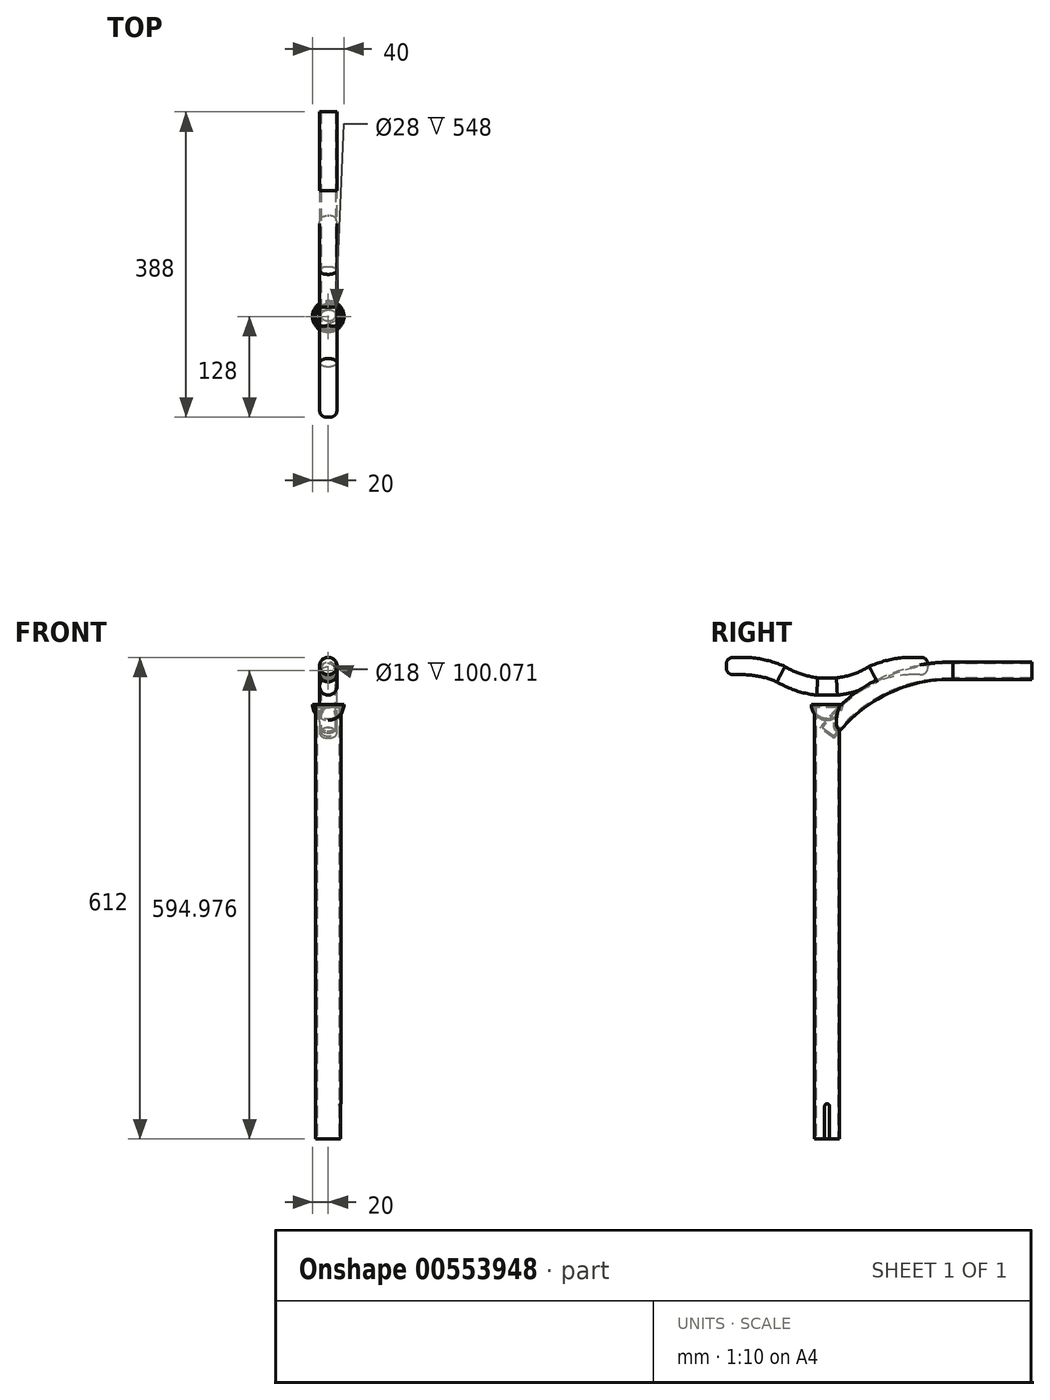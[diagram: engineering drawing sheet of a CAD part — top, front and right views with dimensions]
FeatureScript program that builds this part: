
annotation { "Feature Type Name" : "Feature", "Feature Type Description" : "" }
export const myFeature = defineFeature(function(context is Context, id is Id, definition is map)
    precondition{}
    {
        {
            var Q0;
            Q0=qCreatedBy(makeId("Top.planeOp"),FACE);
            var sketch = newSketch(context, id + "F0", { "sketchPlane" : qUnion([Q0])});
            skCircle(sketch, "E0", {"center": v(0, 0) * mm, "radius": 16 * mm});
            skSolve(sketch);
        }
        {
            var Q0;
            Q0 = qSketchRegion(id + "F0", true);
            extrude(context, id + "F1", {"entities" : qUnion([Q0]), "depth" : 550 * mm, "offsetDistance" : 25 * mm});
        }
        {
            var Q0;
            Q0=makeQuery(id+"F1.opExtrude","CAP_FACE",FACE,{"disambiguationData":[OSD([sQuery(id+"F0.wireOp",EDGE,"E0")])],"isStart":true});
            shell(context, id + "F2", {"entities" : qUnion([Q0]), "thickness" : 2 * mm});
        }
        {
            var Q0;
            Q0=qCreatedBy(makeId("Right.planeOp"),FACE);
            var sketch = newSketch(context, id + "F3", { "sketchPlane" : qUnion([Q0])});
            skLineSegment(sketch, "E1.bottom", {"start": v(-3, 0) * mm, "end": v(3, 0) * mm});
            skLineSegment(sketch, "E1.top", {"start": v(0, 45) * mm, "end": v(0, 45) * mm});
            skLineSegment(sketch, "E1.left", {"start": v(-3, 0) * mm, "end": v(-3, 42) * mm});
            skLineSegment(sketch, "E1.right", {"start": v(3, 0) * mm, "end": v(3, 42) * mm});
            skPoint(sketch, "E2.visualSharp", {"position": v(3, 45) * mm});
            skArc(sketch, "E2.filletArc", {"start": v(3, 42) * mm, "mid": v(2.12, 44.12) * mm, "end": v(0, 45) * mm});
            skPoint(sketch, "E3.visualSharp", {"position": v(-3, 45) * mm});
            skArc(sketch, "E3.filletArc", {"start": v(0, 45) * mm, "mid": v(-2.12, 44.12) * mm, "end": v(-3, 42) * mm});
            skSolve(sketch);
        }
        {
            var Q0;
            Q0 = qSketchRegion(id + "F3", true);
            extrude(context, id + "F4", {"entities" : qUnion([Q0]), "operationType" : NewBodyOperationType.REMOVE, "endBound" : BoundingType.THROUGH_ALL, "depth" : 25 * mm, "offsetDistance" : 25 * mm});
        }
        {
            var Q0;
            Q0=qCreatedBy(makeId("Right.planeOp"),FACE);
            var sketch = newSketch(context, id + "F5", { "sketchPlane" : qUnion([Q0])});
            skArc(sketch, "E4", {"start": v(160, 594.98) * mm, "mid": v(70.4, 574.75) * mm, "end": v(0, 515.76) * mm});
            skLineSegment(sketch, "E5", {"start": v(160, 594.98) * mm, "end": v(260, 594.98) * mm});
            skSolve(sketch);
        }
        {
            var Q0;
            Q0=sQuery(id+"F5.wireOp",VERTEX,"E5.end");
            var Q1;
            Q1=qCreatedBy(makeId("Front.planeOp"),FACE);
            cPlane(context, id + "F6", {"entities" : qUnion([Q0, Q1]), "cplaneType" : CPlaneType.PLANE_POINT, "offset" : 25 * mm, "width" : 150 * mm, "height" : 150 * mm});
        }
        {
            var Q0;
            Q0=qCreatedBy(id+"F6.planeOp",FACE);
            var sketch = newSketch(context, id + "F7", { "sketchPlane" : qUnion([Q0])});
            skCircle(sketch, "E6", {"center": v(0, 594.98) * mm, "radius": 11 * mm});
            skSolve(sketch);
        }
        {
            var Q0;
            Q0 = qSketchRegion(id + "F7", true);
            var Q1;
            Q1 = qConstructionFilter(qBodyType(qCreatedBy(id + "F5" ,EDGE), BodyType.WIRE), ConstructionObject.NO);
            sweep(context, id + "F8", {"operationType" : NewBodyOperationType.ADD, "profiles" : qUnion([Q0]), "path" : qUnion([Q1])});
        }
        {
            var Q0;
            Q0=makeQuery(id+"F8.opSweep","CAP_FACE",FACE,{"disambiguationData":[OSD([sQuery(id+"F5.wireOp",VERTEX,"E5.end"),sQuery(id+"F7.wireOp",EDGE,"E6")])],"isStart":true});
            shell(context, id + "F9", {"entities" : qUnion([Q0]), "thickness" : 2 * mm});
        }
        {
            var Q0;
            Q0=qCreatedBy(makeId("Right.planeOp"),FACE);
            var sketch = newSketch(context, id + "F10", { "sketchPlane" : qUnion([Q0])});
            skLineSegment(sketch, "E7", {"start": v(-128, 601) * mm, "end": v(-108, 601) * mm});
            skArc(sketch, "E8", {"start": v(-58.54, 590.57) * mm, "mid": v(-36.37, 580.26) * mm, "end": v(-12.5, 575) * mm});
            skLineSegment(sketch, "E9", {"start": v(-12.5, 575) * mm, "end": v(0, 575) * mm});
            skLineSegment(sketch, "E10", {"start": v(0, 0) * mm, "end": v(0, 592.35) * mm, "construction": true});
            skArc(sketch, "E11", {"start": v(-58.54, 590.57) * mm, "mid": v(-82.73, 598.36) * mm, "end": v(-108, 601) * mm});
            skLineSegment(sketch, "E12.MirrorCS", {"start": v(12.5, 575) * mm, "end": v(0, 575) * mm});
            skArc(sketch, "E13.MirrorCS", {"start": v(58.54, 590.57) * mm, "mid": v(36.37, 580.26) * mm, "end": v(12.5, 575) * mm});
            skArc(sketch, "E14.MirrorCS", {"start": v(58.54, 590.57) * mm, "mid": v(82.73, 598.36) * mm, "end": v(108, 601) * mm});
            skLineSegment(sketch, "E15.MirrorCS", {"start": v(128, 601) * mm, "end": v(108, 601) * mm});
            skSolve(sketch);
        }
        {
            var Q0;
            Q0=sQuery(id+"F10.wireOp",VERTEX,"E15.MirrorCS.start");
            var Q1;
            Q1=qCreatedBy(id+"F6.planeOp",FACE);
            cPlane(context, id + "F11", {"entities" : qUnion([Q0, Q1]), "cplaneType" : CPlaneType.PLANE_POINT, "offset" : 25 * mm, "width" : 150 * mm, "height" : 150 * mm});
        }
        {
            var Q0;
            Q0=qCreatedBy(id+"F11.planeOp",FACE);
            var sketch = newSketch(context, id + "F12", { "sketchPlane" : qUnion([Q0])});
            skCircle(sketch, "E16", {"center": v(0, 601) * mm, "radius": 11 * mm});
            skSolve(sketch);
        }
        {
            var Q0;
            Q0 = qSketchRegion(id + "F12", true);
            var Q1;
            Q1 = qConstructionFilter(qBodyType(qCreatedBy(id + "F10" ,EDGE), BodyType.WIRE), ConstructionObject.NO);
            sweep(context, id + "F13", {"profiles" : qUnion([Q0]), "path" : qUnion([Q1])});
        }
        {
            var Q0;
            Q0=makeQuery(id+"F13.opSweep","CAP_EDGE",EDGE,{"disambiguationData":[OSD([sQuery(id+"F10.wireOp",VERTEX,"E15.MirrorCS.start"),sQuery(id+"F12.wireOp",EDGE,"E16")])],"isStart":true});
            var Q1;
            Q1=makeQuery(id+"F13.opSweep","CAP_EDGE",EDGE,{"disambiguationData":[OSD([sQuery(id+"F10.wireOp",VERTEX,"E7.start"),sQuery(id+"F12.wireOp",EDGE,"E16")])],"isStart":false});
            fillet(context, id + "F14", {"entities" : qUnion([Q0, Q1]), "radius" : 10 * mm, "tangentPropagation" : true, "rho" : 0.5, "crossSection" : FilletCrossSection.CONIC, "allowEdgeOverflow" : false});
        }
        {
            var Q0;
            Q0=qCreatedBy(makeId("Right.planeOp"),FACE);
            var sketch = newSketch(context, id + "F15", { "sketchPlane" : qUnion([Q0])});
            skArc(sketch, "E17", {"start": v(-20, 552) * mm, "mid": v(-14.14, 537.86) * mm, "end": v(0, 532) * mm});
            skLineSegment(sketch, "E18", {"start": v(0, 552) * mm, "end": v(0, 532) * mm});
            skLineSegment(sketch, "E19", {"start": v(0, 552) * mm, "end": v(-20, 552) * mm});
            skSolve(sketch);
        }
        {
            var Q0;
            Q0 = qSketchRegion(id + "F15", true);
            var Q1;
            Q1=sQuery(id+"F15.wireOp",EDGE,"E18");
            revolve(context, id + "F16", {"surfaceOperationType" : NewSurfaceOperationType.NEW, "entities" : qUnion([Q0]), "axis" : qUnion([Q1]), "revolveType" : RevolveType.FULL});
        }
        {
            var Q0;
            Q0=makeQuery(id+"F16.opRevolve","SWEPT_FACE",FACE,{"disambiguationData":[OSD([sQuery(id+"F15.wireOp",EDGE,"E19")])]});
            shell(context, id + "F17", {"entities" : qUnion([Q0]), "thickness" : 2 * mm});
        }
    });
